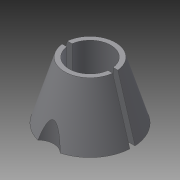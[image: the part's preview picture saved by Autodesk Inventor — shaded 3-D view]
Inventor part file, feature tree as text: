
AUTODESK INVENTOR PART (.ipt)
format: ipt  version: 2014 (Build 180170000, 170)  size: 123,392 bytes
history: native  units: mm
features: sketch x3, extrude x2, revolve x1
ambient origin geometry x8: Origin, YZ Plane, XZ Plane, XY Plane, X Axis, Y Axis, Z Axis, Center Point
bodies: Solid1 (feature_tree)
feature tree (6):
  revolve  "Revolution1"  [1 undecoded]
  extrude  "Extrusion1"  Depth=10.0mm
  extrude  "Extrusion2"  TaperAngle=90.0deg  [1 undecoded]
  sketch  "Sketch1"  dims[d0=3.0mm d1=4.0mm]
  sketch  "Sketch2"  dims[d2=10.0mm d3=7.0mm]
  sketch  "Sketch3"  dims[d4=4.0mm d5=90.0deg d6=1.0mm d7=20.0mm d8=0.0mm d9=0.0mm d10=20.0mm d11=6.0mm d12=0.0mm d13=0.0mm]
note: 2 required parameter values undecoded (feature->parameter linkage not recoverable at this tier; creation-order binding heuristic only, values carry confidence <= 0.55)